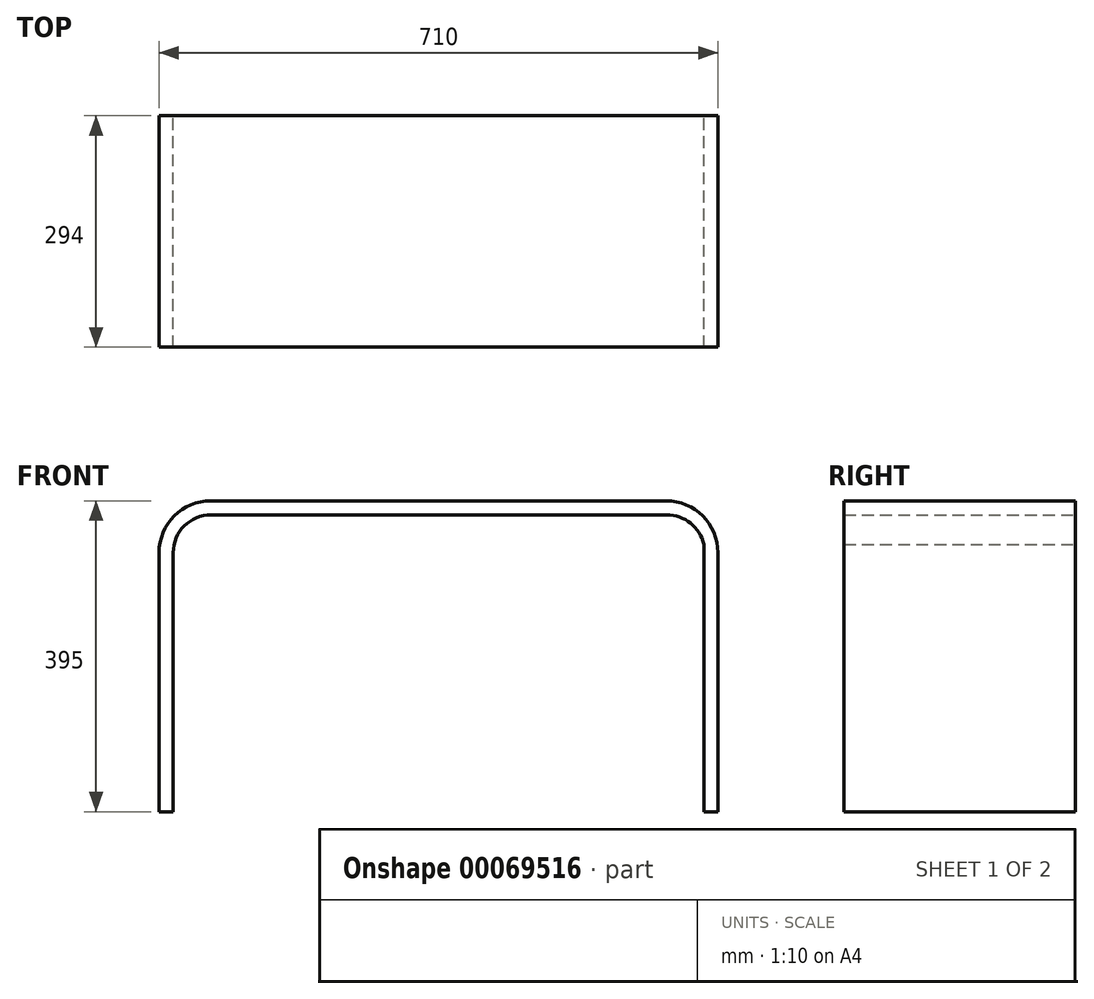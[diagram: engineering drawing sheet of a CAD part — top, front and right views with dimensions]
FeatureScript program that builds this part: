
annotation { "Feature Type Name" : "Feature", "Feature Type Description" : "" }
export const myFeature = defineFeature(function(context is Context, id is Id, definition is map)
    precondition{}
    {
        {
            var Q0;
            Q0=qCreatedBy(makeId("Front.planeOp"),FACE);
            var sketch = newSketch(context, id + "F0", { "sketchPlane" : qUnion([Q0])});
            skLineSegment(sketch, "E0", {"start": v(-1558.32, -76.66) * mm, "end": v(-1558.32, 252.34) * mm});
            skLineSegment(sketch, "E1", {"start": v(-1492.32, 318.34) * mm, "end": v(-914.32, 318.34) * mm});
            skLineSegment(sketch, "E2", {"start": v(-848.32, 252.34) * mm, "end": v(-848.32, -76.66) * mm});
            skLineSegment(sketch, "E3", {"start": v(-1558.32, -76.66) * mm, "end": v(-1540.32, -76.66) * mm});
            skLineSegment(sketch, "E4", {"start": v(-1540.32, -76.66) * mm, "end": v(-1540.32, 252.34) * mm});
            skLineSegment(sketch, "E5", {"start": v(-1492.32, 300.34) * mm, "end": v(-913.15, 300.34) * mm});
            skPoint(sketch, "E6.visualSharp", {"position": v(-1558.32, 318.34) * mm});
            skArc(sketch, "E6.filletArc", {"start": v(-1492.32, 318.34) * mm, "mid": v(-1539, 299.01) * mm, "end": v(-1558.32, 252.34) * mm});
            skPoint(sketch, "E7.visualSharp", {"position": v(-1540.32, 300.34) * mm});
            skArc(sketch, "E7.filletArc", {"start": v(-1492.32, 300.34) * mm, "mid": v(-1526.26, 286.28) * mm, "end": v(-1540.32, 252.34) * mm});
            skPoint(sketch, "E8.visualSharp", {"position": v(-848.32, 318.34) * mm});
            skArc(sketch, "E8.filletArc", {"start": v(-848.32, 252.34) * mm, "mid": v(-867.65, 299.01) * mm, "end": v(-914.32, 318.34) * mm});
            skPoint(sketch, "E9.visualSharp", {"position": v(-887.72, 300.34) * mm});
            skArc(sketch, "E9.filletArc", {"start": v(-866.32, 262.88) * mm, "mid": v(-883.17, 289.82) * mm, "end": v(-913.15, 300.34) * mm});
            skLineSegment(sketch, "E10", {"start": v(-848.32, -76.66) * mm, "end": v(-866.32, -76.66) * mm});
            skLineSegment(sketch, "E11", {"start": v(-866.32, 262.88) * mm, "end": v(-866.32, -76.66) * mm});
            skSolve(sketch);
        }
        {
            var Q0;
            Q0 = qSketchRegion(id + "F0", true);
            extrude(context, id + "F1", {"entities" : qUnion([Q0]), "endBound" : BoundingType.SYMMETRIC, "depth" : 294 * mm});
        }
    });
